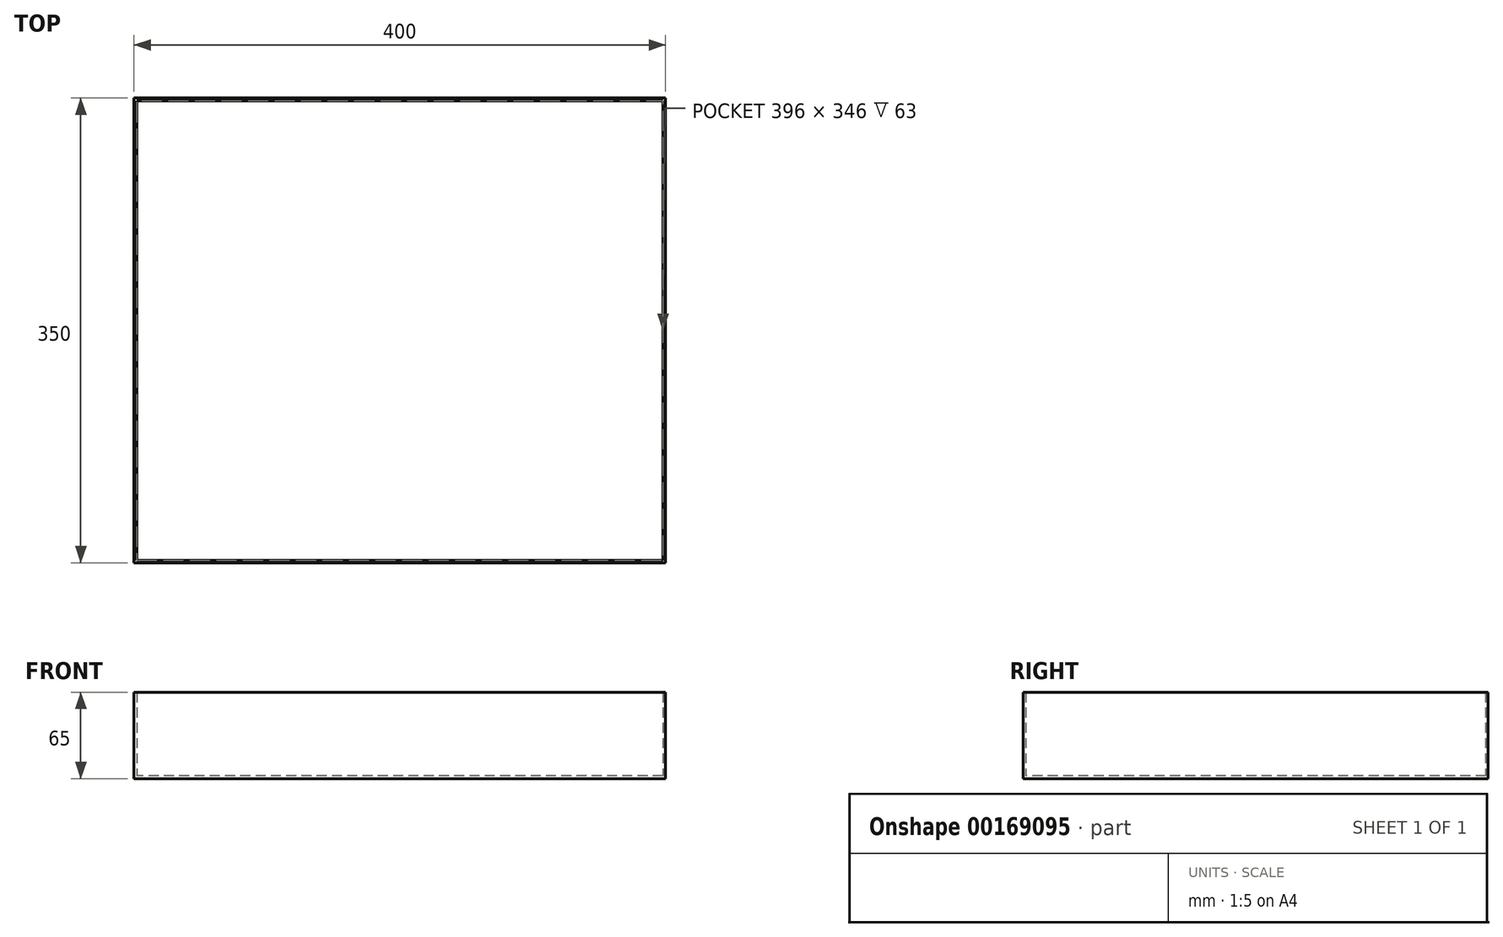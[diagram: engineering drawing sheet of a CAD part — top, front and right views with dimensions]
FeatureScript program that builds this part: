
annotation { "Feature Type Name" : "Feature", "Feature Type Description" : "" }
export const myFeature = defineFeature(function(context is Context, id is Id, definition is map)
    precondition{}
    {
        {
            var Q0;
            Q0=qCreatedBy(makeId("Top.planeOp"),FACE);
            var sketch = newSketch(context, id + "F0", { "sketchPlane" : qUnion([Q0])});
            skLineSegment(sketch, "E0.bottom", {"start": v(200, -175) * mm, "end": v(-200, -175) * mm});
            skLineSegment(sketch, "E0.top", {"start": v(200, 175) * mm, "end": v(-200, 175) * mm});
            skLineSegment(sketch, "E0.left", {"start": v(200, -175) * mm, "end": v(200, 175) * mm});
            skLineSegment(sketch, "E0.right", {"start": v(-200, -175) * mm, "end": v(-200, 175) * mm});
            skPoint(sketch, "E0.middle", {"position": v(0, 0) * mm});
            skLineSegment(sketch, "E1.bottom", {"start": v(198, 173) * mm, "end": v(-198, 173) * mm});
            skLineSegment(sketch, "E1.top", {"start": v(198, -173) * mm, "end": v(-198, -173) * mm});
            skLineSegment(sketch, "E1.left", {"start": v(198, 173) * mm, "end": v(198, -173) * mm});
            skLineSegment(sketch, "E1.right", {"start": v(-198, 173) * mm, "end": v(-198, -173) * mm});
            skSolve(sketch);
        }
        {
            var Q0;
            Q0=qSketchRegion(id+"F0",true);
            extrude(context, id + "F1", {"entities" : qUnion([Q0]), "depth" : 65 * mm});
        }
        {
            var Q0;
            Q0=makeQuery(id+"F0.imprint","IMPRINT",FACE,{"disambiguationData":[TD([[makeQuery(id+"F0.imprint","IMPRINT",EDGE,{"derivedFrom":sQuery(id+"F0.wireOp",EDGE,"E1.bottom")}),1.0]])]});
            extrude(context, id + "F2", {"entities" : qUnion([Q0]), "operationType" : NewBodyOperationType.ADD, "depth" : 2 * mm});
        }
    });
